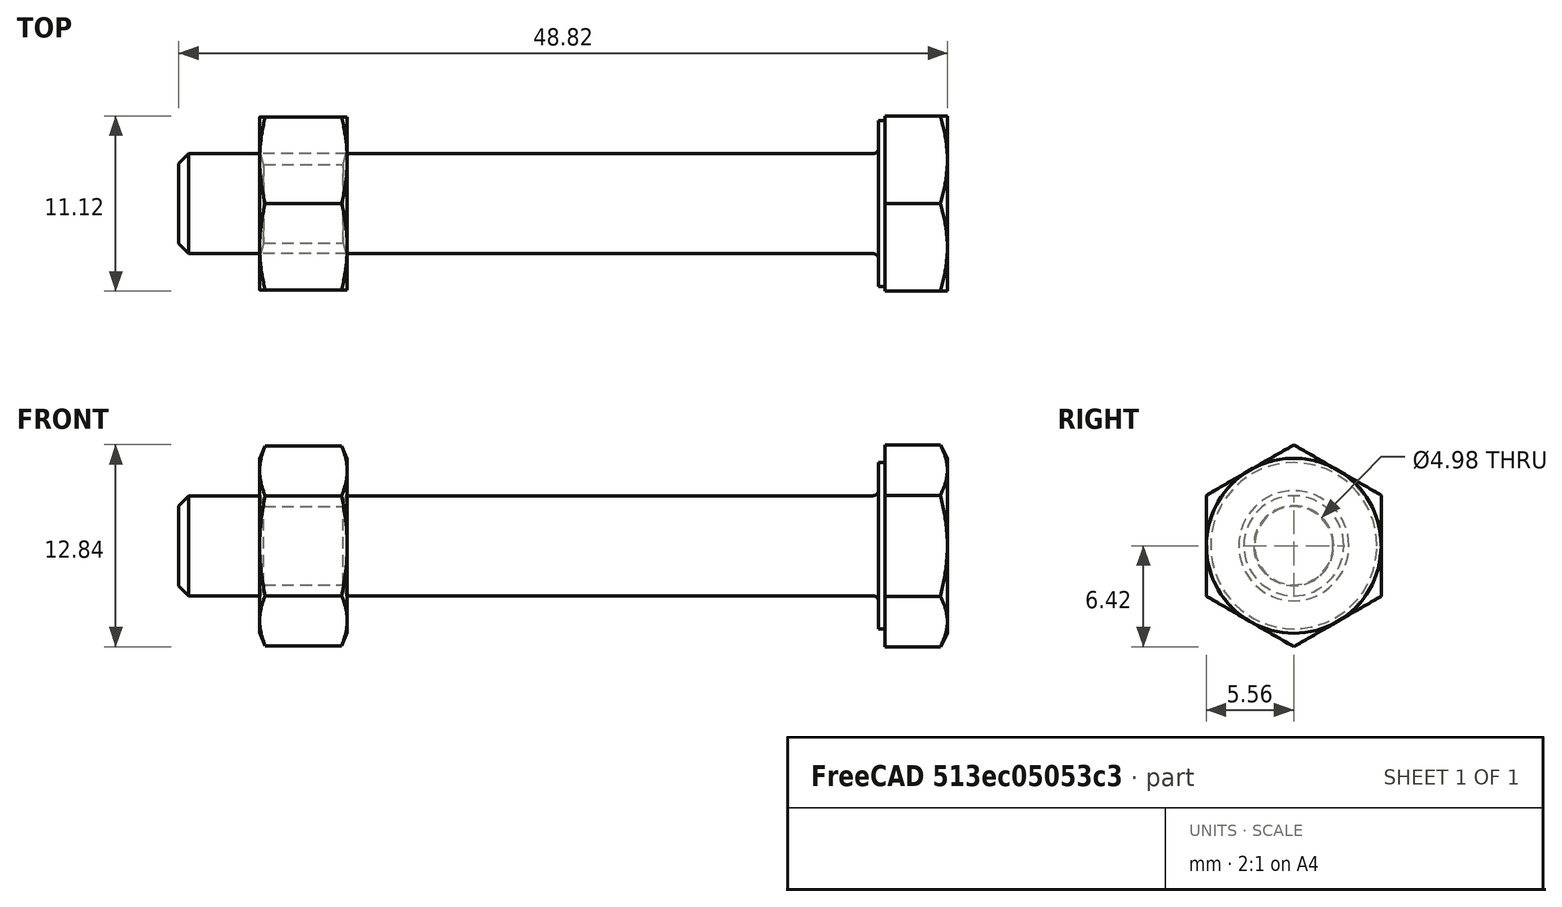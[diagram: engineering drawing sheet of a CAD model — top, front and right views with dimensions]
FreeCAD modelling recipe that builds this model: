
FCSTD DOCUMENT  (FreeCAD 0.20R29177 +426 (Git))
Label: ASM_Base
License: All rights reserved
LicenseURL: http://en.wikipedia.org/wiki/All_rights_reserved
objects: App::Link×10, App::DocumentObjectGroup×3, Part::FeaturePython×2, PartDesign::CoordinateSystem×1, App::FeaturePython×1, App::Part×1
note: 3 computed .brp shape members not serialized (recipe doc carries the construction recipe); baked Part::Feature solids carry a one-line shape summary decoded from their .brp
EXTERNAL_REF file=PillowBlock.FCStd obj=Sketch001
EXTERNAL_REF file=StrutChannelHalf.FCStd obj=LCS_Face
EXTERNAL_REF file=StrutChannelHalf.FCStd obj=Assembly
EXTERNAL_REF file=PillowBlock.FCStd obj=LCS_Origin
EXTERNAL_REF file=PillowBlock.FCStd obj=Assembly
EXTERNAL_REF file=PipeNipple.FCStd obj=LCS_root
EXTERNAL_REF file=PipeNipple.FCStd obj=Body
EXTERNAL_REF file=Arm.FCStd obj=LCS_Center
EXTERNAL_REF file=PipeNipple.FCStd obj=LCS_end
EXTERNAL_REF file=Arm.FCStd obj=Part
EXTERNAL_REF file=SlipRing.FCStd obj=LCS_Origin
EXTERNAL_REF file=SlipRing.FCStd obj=Assembly
EXTERNAL_REF file=Arm.FCStd obj=LCS_End2
EXTERNAL_REF file=Board.FCStd obj=LCS_Center
EXTERNAL_REF file=Board.FCStd obj=Part
EXTERNAL_REF file=ASM_Stepper.FCStd obj=LCS_Origin
EXTERNAL_REF file=ASM_Stepper.FCStd obj=Assembly
EXTERNAL_REF file=Platform.FCStd obj=LCS_Origin
EXTERNAL_REF file=Platform.FCStd obj=Assembly
EXTERNAL_REF file=Platform.FCStd obj=Pad
EXTERNAL_REF file=PlayStation5.FCStd obj=LCS_Origin
EXTERNAL_REF file=PlayStation5.FCStd obj=Assembly

FEATURE [App::DocumentObjectGroup] Parts
FEATURE [PartDesign::CoordinateSystem] LCS_Origin
  AttacherType = Attacher::AttachEngine3D
  MapMode = 2
  Support = -> [X_Axis]
FEATURE [App::DocumentObjectGroup] Constraints
FEATURE [App::FeaturePython] Variables  # WARN: FeaturePython — macro-defined, semantics opaque (R4)
  PillowBlockBoltSpacing = 102.01
  Type = App::PropertyContainer
  expr: PillowBlockBoltSpacing = <<PillowBlock>>#<<PadSketch>>.Constraints.MountHoleSpacing
FEATURE [App::DocumentObjectGroup] Configurations
FEATURE [App::Link] StrutChannelHalf_1
  AttachedBy = #LCS_Face
  AttachedTo = Parent Assembly#LCS_Origin
  AttachmentOffset = pos=(-51.005,0,0) rot=(1,0,0;4.71239rad)
  LinkPlacement = pos=(-51.005,4.6e-15,20.64) rot=(1,0,0;4.71239rad)
  LinkedObject = -> <external StrutChannelHalf.FCStd>#Assembly
  Placement = pos=(-51.005,4.6e-15,20.64) rot=(1,0,0;4.71239rad)
  SolverId = Asm4EE
  expr: .AttachmentOffset.Base.x = <<Variables>>.PillowBlockBoltSpacing / -2
  expr: Placement = LCS_Origin.Placement * AttachmentOffset * StrutChannelHalf#LCS_Face.Placement ^ -1
FEATURE [App::Link] StrutChannelHalf_002
  AttachedBy = #LCS_Face
  AttachedTo = Parent Assembly#LCS_Origin
  AttachmentOffset = pos=(51.005,0,0) rot=(1,0,0;4.71239rad)
  LinkPlacement = pos=(51.005,4.6e-15,20.64) rot=(1,0,0;4.71239rad)
  LinkedObject = -> <external StrutChannelHalf.FCStd>#Assembly
  Placement = pos=(51.005,4.6e-15,20.64) rot=(1,0,0;4.71239rad)
  SolverId = Asm4EE
  expr: .AttachmentOffset.Base.x = <<Variables>>.PillowBlockBoltSpacing / 2
  expr: Placement = LCS_Origin.Placement * AttachmentOffset * StrutChannelHalf#LCS_Face.Placement ^ -1
FEATURE [App::Link] PillowBlock
  AttachedBy = #LCS_Origin
  AttachedTo = Parent Assembly#LCS_Origin
  AttachmentOffset = pos=(0,0,0) rot=(1,0,0;3.14159rad)
  LinkPlacement = pos=(0,0,0) rot=(1,0,0;3.14159rad)
  LinkedObject = -> <external PillowBlock.FCStd>#Assembly
  Placement = pos=(0,0,0) rot=(1,0,0;3.14159rad)
  SolverId = Asm4EE
  expr: Placement = LCS_Origin.Placement * AttachmentOffset * PillowBlock#LCS_Origin.Placement ^ -1
FEATURE [App::Link] Spindle
  AttachedBy = #LCS_root
  AttachedTo = Parent Assembly#LCS_Origin
  AttachmentOffset = pos=(0,0,10) rot=(1,0,0;3.14159rad)
  LinkPlacement = pos=(0,0,10) rot=(1,0,0;3.14159rad)
  LinkedObject = -> <external PipeNipple.FCStd>#Body
  Placement = pos=(0,0,10) rot=(1,0,0;3.14159rad)
  SolverId = Asm4EE
  expr: Placement = LCS_Origin.Placement * AttachmentOffset * PipeNipple#LCS_root.Placement ^ -1
FEATURE [App::Link] Arm
  AttachedBy = #LCS_Center
  AttachedTo = Spindle#LCS_end
  AttachmentOffset = pos=(0,-350,-14) rot=(-0.57735,-0.57735,0.57735;4.18879rad)
  LinkPlacement = pos=(0,350,-116) rot=(-0.57735,-0.57735,-0.57735;2.0944rad)
  LinkedObject = -> <external Arm.FCStd>#Part
  Placement = pos=(0,350,-116) rot=(-0.57735,-0.57735,-0.57735;2.0944rad)
  SolverId = Asm4EE
  expr: Placement = Spindle.Placement * PipeNipple#LCS_end.Placement * AttachmentOffset * Arm#LCS_Center.Placement ^ -1
FEATURE [Part::FeaturePython] Screw  label="1/4inx1 3/4in-Screw"  # Fasteners workbench fastener (typed FeaturePython)
  AttachedBy = Origin
  AttachedTo = Spindle#LCS_end
  AttachmentOffset = pos=(17,0,-16) rot=(0,-1,0;4.71239rad)
  Placement = pos=(17,-1.52e-14,-114) rot=(-0.707107,0,-0.707107;3.14159rad)
  SolverId = Asm4EE
  diameter = 1
  invert = false
  leftHanded = false
  length = 7
  lengthCustom = 44.45
  matchOuter = false
  offset = 0
  thread = false
  type = 1
  expr: Placement = Spindle.Placement * PipeNipple#LCS_end.Placement * AttachmentOffset
FEATURE [Part::FeaturePython] Nut  label="1/4in-Nut"  # Fasteners workbench fastener (typed FeaturePython)
  Placement = pos=(-22.315,-1.52e-14,-114) rot=(0,1,0;1.5708rad)
  baseObject = -> Screw [Edge41]
  diameter = 1
  invert = false
  leftHanded = false
  matchOuter = false
  offset = 4.5
  thread = false
  type = 5
FEATURE [App::Link] SlipRing
  AttachedBy = #LCS_Origin
  AttachedTo = Spindle#LCS_root
  LinkPlacement = pos=(0,0,10) rot=(1,0,0;3.14159rad)
  LinkedObject = -> <external SlipRing.FCStd>#Assembly
  Placement = pos=(0,0,10) rot=(1,0,0;3.14159rad)
  SolverId = Asm4EE
  expr: Placement = Spindle.Placement * PipeNipple#LCS_root.Placement * AttachmentOffset * SlipRing#LCS_Origin.Placement ^ -1
FEATURE [App::Link] MotorBoard
  AttachedBy = #LCS_Center
  AttachedTo = Arm#LCS_End2
  AttachmentOffset = pos=(11,0,-9.5) rot=(0.57735,0.57735,0.57735;2.0944rad)
  LinkPlacement = pos=(1.662e-13,-409.5,-105) rot=(0,0,1;0rad)
  LinkedObject = -> <external Board.FCStd>#Part
  Placement = pos=(1.662e-13,-409.5,-105) rot=(0,0,1;0rad)
  SolverId = Asm4EE
  expr: Placement = Arm.Placement * Arm#LCS_End2.Placement * AttachmentOffset * Board#LCS_Center.Placement ^ -1
FEATURE [App::Link] ASM_Stepper
  AttachedBy = #LCS_Origin
  AttachedTo = MotorBoard#LCS_Center
  AttachmentOffset = pos=(0,-9.5,13) rot=(1,0,0;1.5708rad)
  LinkPlacement = pos=(1.611e-13,-419,-92) rot=(1,0,0;1.5708rad)
  LinkedObject = -> <external ASM_Stepper.FCStd>#Assembly
  Placement = pos=(1.611e-13,-419,-92) rot=(1,0,0;1.5708rad)
  SolverId = Asm4EE
  expr: Placement = MotorBoard.Placement * Board#LCS_Center.Placement * AttachmentOffset * ASM_Stepper#LCS_Origin.Placement ^ -1
FEATURE [App::Link] Platform
  AttachedBy = #LCS_Origin
  AttachedTo = Arm#LCS_End2
  AttachmentOffset = pos=(19.05,0,170) rot=(0.57735,0.57735,0.57735;2.0944rad)
  LinkPlacement = pos=(1.246e-13,-230,-96.95) rot=(0,0,1;0rad)
  LinkedObject = -> <external Platform.FCStd>#Assembly
  Placement = pos=(1.246e-13,-230,-96.95) rot=(0,0,1;0rad)
  SolverId = Asm4EE
  expr: Placement = Arm.Placement * Arm#LCS_End2.Placement * AttachmentOffset * Platform#LCS_Origin.Placement ^ -1
FEATURE [App::Link] PlayStation5
  AttachedBy = #LCS_Origin
  AttachedTo = Platform#LCS_Origin
  AttachmentOffset = pos=(0,0,6.35) rot=(0,0,1;1.5708rad)
  LinkPlacement = pos=(1.221e-13,-230,-90.6) rot=(0,0,1;1.5708rad)
  LinkedObject = -> <external PlayStation5.FCStd>#Assembly
  Placement = pos=(1.221e-13,-230,-90.6) rot=(0,0,1;1.5708rad)
  SolverId = Asm4EE
  expr: .AttachmentOffset.Base.z = <<Platform>>#<<Pad>>.Length
  expr: Placement = Platform.Placement * Platform#LCS_Origin.Placement * AttachmentOffset * PlayStation5#LCS_Origin.Placement ^ -1
FEATURE [App::Part] Assembly
  AssemblyType = Part::Link
  Group = -> [LCS_Origin,Constraints,Variables,Configurations,StrutChannelHalf_1,StrutChannelHalf_002,PillowBlock,Spindle,Arm,Screw,Nut,SlipRing,MotorBoard,ASM_Stepper,Platform,PlayStation5]
  Origin = -> Origin
  Type = Assembly

RESOLVED EXTERNAL PARTS (link-assembly join: the EXTERNAL_REF files above that resolve inside this repo's crawl, each included once):
---- part ASM_Stepper.FCStd = doc fcstd_8e194f77de06 ----
FCSTD DOCUMENT  (FreeCAD 0.20R29177 +426 (Git))
Label: ASM_Stepper
License: All rights reserved
LicenseURL: http://en.wikipedia.org/wiki/All_rights_reserved
objects: App::Link×4, App::DocumentObjectGroup×3, PartDesign::CoordinateSystem×1, App::FeaturePython×1, App::Part×1
note: 1 computed .brp shape members not serialized (recipe doc carries the construction recipe); baked Part::Feature solids carry a one-line shape summary decoded from their .brp
EXTERNAL_REF file=Stepper17BracketFlat.FCStd obj=LCS_Mount
EXTERNAL_REF file=Stepper17BracketFlat.FCStd obj=Assembly
EXTERNAL_REF file=Stepper17.FCStd obj=LCS_mount
EXTERNAL_REF file=Stepper17BracketFlat.FCStd obj=LCS_Origin
EXTERNAL_REF file=Stepper17.FCStd obj=Body
EXTERNAL_REF file=FlangeHub5mm.FCStd obj=LCS_Origin
EXTERNAL_REF file=FlangeHub5mm.FCStd obj=Assembly
EXTERNAL_REF file=Wheel.FCStd obj=LCS_Origin
EXTERNAL_REF file=Wheel.FCStd obj=Assembly

FEATURE [App::DocumentObjectGroup] Parts
FEATURE [PartDesign::CoordinateSystem] LCS_Origin
  AttacherType = Attacher::AttachEngine3D
  MapMode = 2
  Support = -> [X_Axis]
FEATURE [App::DocumentObjectGroup] Constraints
FEATURE [App::FeaturePython] Variables  # WARN: FeaturePython — macro-defined, semantics opaque (R4)
  Type = App::PropertyContainer
FEATURE [App::DocumentObjectGroup] Configurations
FEATURE [App::Link] Stepper17BracketFlat
  AttachedBy = #LCS_Mount
  AttachedTo = Parent Assembly#LCS_Origin
  LinkPlacement = pos=(0,53.75,0) rot=(0,0,1;0rad)
  LinkedObject = -> <external Stepper17BracketFlat.FCStd>#Assembly
  Placement = pos=(0,53.75,0) rot=(0,0,1;0rad)
  SolverId = Asm4EE
  expr: Placement = LCS_Origin.Placement * AttachmentOffset * Stepper17BracketFlat#LCS_Mount.Placement ^ -1
FEATURE [App::Link] Stepper
  AttachedBy = #LCS_mount
  AttachedTo = Stepper17BracketFlat#LCS_Origin
  AttachmentOffset = pos=(0,0,0) rot=(0,1,0;3.14159rad)
  LinkPlacement = pos=(0,53.75,0) rot=(0,1,0;3.14159rad)
  LinkedObject = -> <external Stepper17.FCStd>#Body
  Placement = pos=(0,53.75,0) rot=(0,1,0;3.14159rad)
  SolverId = Asm4EE
  expr: Placement = Stepper17BracketFlat.Placement * Stepper17BracketFlat#LCS_Origin.Placement * AttachmentOffset * Stepper17#LCS_mount.Placement ^ -1
FEATURE [App::Link] FlangeHub5mm
  AttachedBy = #LCS_Origin
  AttachedTo = Stepper#LCS_mount
  AttachmentOffset = pos=(0,0,-14) rot=(1,0,0;3.14159rad)
  LinkPlacement = pos=(-1.7e-15,53.75,14) rot=(0,0,-1;3.14159rad)
  LinkedObject = -> <external FlangeHub5mm.FCStd>#Assembly
  Placement = pos=(-1.7e-15,53.75,14) rot=(0,0,-1;3.14159rad)
  SolverId = Asm4EE
  expr: Placement = Stepper.Placement * Stepper17#LCS_mount.Placement * AttachmentOffset * FlangeHub5mm#LCS_Origin.Placement ^ -1
FEATURE [App::Link] Wheel
  AttachedBy = #LCS_Origin
  AttachedTo = FlangeHub5mm#LCS_Origin
  AttachmentOffset = pos=(0,0,0) rot=(0,1,0;3.14159rad)
  LinkPlacement = pos=(-1.7e-15,53.75,14) rot=(1,0,0;3.14159rad)
  LinkedObject = -> <external Wheel.FCStd>#Assembly
  Placement = pos=(-1.7e-15,53.75,14) rot=(1,0,0;3.14159rad)
  SolverId = Asm4EE
  expr: Placement = FlangeHub5mm.Placement * FlangeHub5mm#LCS_Origin.Placement * AttachmentOffset * Wheel#LCS_Origin.Placement ^ -1
FEATURE [App::Part] Assembly
  AssemblyType = Part::Link
  Group = -> [LCS_Origin,Constraints,Variables,Configurations,Stepper17BracketFlat,Stepper,FlangeHub5mm,Wheel]
  Origin = -> Origin
  Type = Assembly
---- part Arm.FCStd = doc fcstd_95bc69fd2989 ----
FCSTD DOCUMENT  (FreeCAD 0.20R29177 +426 (Git))
Label: Arm
License: All rights reserved
LicenseURL: http://en.wikipedia.org/wiki/All_rights_reserved
objects: PartDesign::CoordinateSystem×3, Sketcher::SketchObject×1, App::FeaturePython×1, PartDesign::Pad×1, PartDesign::Body×1, App::Part×1
note: 7 computed .brp shape members not serialized (recipe doc carries the construction recipe); baked Part::Feature solids carry a one-line shape summary decoded from their .brp

FEATURE [Sketcher::SketchObject] Sketch
  FullyConstrained = true
  MapMode = 5
  Support = -> [XY_Plane001]
  expr: Constraints[16] = <<Variables>>.FilletRadius
  expr: Constraints[18] = <<Variables>>.Dim1
  expr: Constraints[19] = <<Variables>>.Dim2
  sketch-geometry (9):
    g0: LineSegment StartX=-19.05 StartY=9.025 StartZ=0 EndX=-19.05 EndY=-9.025 EndZ=0
    g1: LineSegment StartX=-18.55 StartY=-9.525 StartZ=0 EndX=18.55 EndY=-9.525 EndZ=0
    g2: LineSegment StartX=19.05 StartY=-9.025 StartZ=0 EndX=19.05 EndY=9.025 EndZ=0
    g3: LineSegment StartX=18.55 StartY=9.525 StartZ=0 EndX=-18.55 EndY=9.525 EndZ=0
    g4: GeomPoint X=0 Y=0 Z=0
    g5: ArcOfCircle CenterX=-18.55 CenterY=9.025 CenterZ=0 NormalX=0 NormalY=0 NormalZ=1 AngleXU=0 Radius=0.5 StartAngle=1.5708 EndAngle=3.14159
    g6: ArcOfCircle CenterX=-18.55 CenterY=-9.025 CenterZ=0 NormalX=0 NormalY=0 NormalZ=1 AngleXU=0 Radius=0.5 StartAngle=3.14159 EndAngle=4.71239
    g7: ArcOfCircle CenterX=18.55 CenterY=9.025 CenterZ=0 NormalX=0 NormalY=0 NormalZ=1 AngleXU=0 Radius=0.5 StartAngle=1.95e-14 EndAngle=1.5708
    g8: ArcOfCircle CenterX=18.55 CenterY=-9.025 CenterZ=0 NormalX=0 NormalY=0 NormalZ=1 AngleXU=0 Radius=0.5 StartAngle=4.71239 EndAngle=6.28319
  constraints (20):
    c: Horizontal(g1)
    c: Horizontal(g3)
    c: Vertical(g0)
    c: Vertical(g2)
    c: Coincident(g4,g-1)
    c: Tangent(g3,g5) = -1.5708
    c: Tangent(g0,g5) = -1.5708
    c: Tangent(g0,g6) = -1.5708
    c: Tangent(g1,g6) = -1.5708
    c: Tangent(g3,g7) = -1.5708
    c: Tangent(g2,g7) = -1.5708
    c: Tangent(g2,g8) = -1.5708
    c: Tangent(g1,g8) = -1.5708
    c: Equal(g8,g7)
    c: Equal(g7,g5)
    c: Equal(g5,g6)
    c: Radius(g7) = 0.5
    c: Symmetric(g7,g6,g4)
    c: DistanceY(g1,g3) = 19.05
    c: DistanceX(g0,g2) = 38.1
FEATURE [App::FeaturePython] Variables  # WARN: FeaturePython — macro-defined, semantics opaque (R4)
  Dim1 = 19.05
  Dim2 = 38.1
  FilletRadius = 0.5
  Length = 1500
  Type = App::PropertyContainer
FEATURE [PartDesign::Pad] Pad
  Direction = (0,0,1)
  Length = 1500
  Length2 = 10
  Midplane = true
  Profile = -> Sketch
  ReferenceAxis = -> Sketch [N_Axis]
  Type = 0
  expr: Length = <<Variables>>.Length
FEATURE [PartDesign::Body] Body
  Group = -> [Sketch,Pad]
  Origin = -> Origin001
  Tip = -> Pad
FEATURE [PartDesign::CoordinateSystem] LCS_Center
  AttacherType = Attacher::AttachEngine3D
  MapMode = 2
  Support = -> [XY_Plane]
FEATURE [PartDesign::CoordinateSystem] LCS_End1
  AttacherType = Attacher::AttachEngine3D
  AttachmentOffset = pos=(0,0,750) rot=(0,0,1;0rad)
  MapMode = 2
  Placement = pos=(0,0,750) rot=(0,0,1;0rad)
  Support = -> [XY_Plane]
  expr: .AttachmentOffset.Base.z = <<Variables>>.Length / 2
FEATURE [PartDesign::CoordinateSystem] LCS_End2
  AttacherType = Attacher::AttachEngine3D
  AttachmentOffset = pos=(0,0,-750) rot=(0,0,1;0rad)
  MapMode = 2
  Placement = pos=(0,0,-750) rot=(0,0,1;0rad)
  Support = -> [XY_Plane]
  expr: .AttachmentOffset.Base.z = <<Variables>>.Length / -2
FEATURE [App::Part] Part
  Group = -> [Body,Variables,LCS_Center,LCS_End1,LCS_End2]
  Origin = -> Origin
  Type = Asm4::VariantLink
---- part Board.FCStd = doc fcstd_57f5a6b6b108 ----
FCSTD DOCUMENT  (FreeCAD 0.20R29177 +426 (Git))
Label: Board
License: All rights reserved
LicenseURL: http://en.wikipedia.org/wiki/All_rights_reserved
objects: PartDesign::CoordinateSystem×3, Sketcher::SketchObject×1, App::FeaturePython×1, PartDesign::Pad×1, PartDesign::Body×1, App::Part×1
note: 7 computed .brp shape members not serialized (recipe doc carries the construction recipe); baked Part::Feature solids carry a one-line shape summary decoded from their .brp

FEATURE [Sketcher::SketchObject] Sketch
  FullyConstrained = true
  MapMode = 5
  Support = -> [XY_Plane001]
  expr: Constraints[16] = <<Variables>>.FilletRadius
  expr: Constraints[18] = <<Variables>>.Dim1
  expr: Constraints[19] = <<Variables>>.Dim2
  sketch-geometry (9):
    g0: LineSegment StartX=-19.05 StartY=9.025 StartZ=0 EndX=-19.05 EndY=-9.025 EndZ=0
    g1: LineSegment StartX=-18.55 StartY=-9.525 StartZ=0 EndX=18.55 EndY=-9.525 EndZ=0
    g2: LineSegment StartX=19.05 StartY=-9.025 StartZ=0 EndX=19.05 EndY=9.025 EndZ=0
    g3: LineSegment StartX=18.55 StartY=9.525 StartZ=0 EndX=-18.55 EndY=9.525 EndZ=0
    g4: GeomPoint X=0 Y=0 Z=0
    g5: ArcOfCircle CenterX=-18.55 CenterY=9.025 CenterZ=0 NormalX=0 NormalY=0 NormalZ=1 AngleXU=0 Radius=0.5 StartAngle=1.5708 EndAngle=3.14159
    g6: ArcOfCircle CenterX=-18.55 CenterY=-9.025 CenterZ=0 NormalX=0 NormalY=0 NormalZ=1 AngleXU=0 Radius=0.5 StartAngle=3.14159 EndAngle=4.71239
    g7: ArcOfCircle CenterX=18.55 CenterY=9.025 CenterZ=0 NormalX=0 NormalY=0 NormalZ=1 AngleXU=0 Radius=0.5 StartAngle=-8.4555e-12 EndAngle=1.5708
    g8: ArcOfCircle CenterX=18.55 CenterY=-9.025 CenterZ=0 NormalX=0 NormalY=0 NormalZ=1 AngleXU=0 Radius=0.5 StartAngle=4.71239 EndAngle=6.28319
  constraints (20):
    c: Horizontal(g1)
    c: Horizontal(g3)
    c: Vertical(g0)
    c: Vertical(g2)
    c: Coincident(g4,g-1)
    c: Tangent(g3,g5) = -1.5708
    c: Tangent(g0,g5) = -1.5708
    c: Tangent(g0,g6) = -1.5708
    c: Tangent(g1,g6) = -1.5708
    c: Tangent(g3,g7) = -1.5708
    c: Tangent(g2,g7) = -1.5708
    c: Tangent(g2,g8) = -1.5708
    c: Tangent(g1,g8) = -1.5708
    c: Equal(g8,g7)
    c: Equal(g7,g5)
    c: Equal(g5,g6)
    c: Radius(g7) = 0.5
    c: Symmetric(g7,g6,g4)
    c: DistanceY(g1,g3) = 19.05
    c: DistanceX(g0,g2) = 38.1
FEATURE [App::FeaturePython] Variables  # WARN: FeaturePython — macro-defined, semantics opaque (R4)
  Dim1 = 19.05
  Dim2 = 38.1
  FilletRadius = 0.5
  Length = 60
  Type = App::PropertyContainer
FEATURE [PartDesign::Pad] Pad
  Direction = (0,0,1)
  Length = 60
  Length2 = 10
  Midplane = true
  Profile = -> Sketch
  ReferenceAxis = -> Sketch [N_Axis]
  Type = 0
  expr: Length = <<Variables>>.Length
FEATURE [PartDesign::Body] Body
  Group = -> [Sketch,Pad]
  Origin = -> Origin001
  Tip = -> Pad
FEATURE [PartDesign::CoordinateSystem] LCS_Center
  AttacherType = Attacher::AttachEngine3D
  MapMode = 2
  Support = -> [XY_Plane]
FEATURE [PartDesign::CoordinateSystem] LCS_End1
  AttacherType = Attacher::AttachEngine3D
  AttachmentOffset = pos=(0,0,30) rot=(0,0,1;0rad)
  MapMode = 2
  Placement = pos=(0,0,30) rot=(0,0,1;0rad)
  Support = -> [XY_Plane]
  expr: .AttachmentOffset.Base.z = <<Variables>>.Length / 2
FEATURE [PartDesign::CoordinateSystem] LCS_End2
  AttacherType = Attacher::AttachEngine3D
  AttachmentOffset = pos=(0,0,-30) rot=(0,0,1;0rad)
  MapMode = 2
  Placement = pos=(0,0,-30) rot=(0,0,1;0rad)
  Support = -> [XY_Plane]
  expr: .AttachmentOffset.Base.z = <<Variables>>.Length / -2
FEATURE [App::Part] Part
  Group = -> [Body,Variables,LCS_Center,LCS_End1,LCS_End2]
  Origin = -> Origin
  Type = Asm4::VariantLink
---- part PillowBlock.FCStd = doc fcstd_4e686e80bc07 ----
FCSTD DOCUMENT  (FreeCAD 0.20R29177 +426 (Git))
Label: PillowBlock
License: All rights reserved
LicenseURL: http://en.wikipedia.org/wiki/All_rights_reserved
objects: App::DocumentObjectGroup×4, Part::FeaturePython×4, Sketcher::SketchObject×2, PartDesign::Revolution×1, PartDesign::Pad×1, PartDesign::Body×1, PartDesign::CoordinateSystem×1, App::FeaturePython×1, App::Part×1
note: 12 computed .brp shape members not serialized (recipe doc carries the construction recipe); baked Part::Feature solids carry a one-line shape summary decoded from their .brp

FEATURE [Sketcher::SketchObject] Sketch
  FullyConstrained = true
  MapMode = 5
  Placement = pos=(0,0,0) rot=(1,0,0;1.5708rad)
  Support = -> [XZ_Plane]
  sketch-geometry (6):
    g0: LineSegment StartX=19.05 StartY=0 StartZ=0 EndX=19.05 EndY=51.2064 EndZ=0
    g1: LineSegment StartX=43.4 StartY=36.068 StartZ=0 EndX=51.05 EndY=0 EndZ=0
    g2: LineSegment StartX=51.05 StartY=0 StartZ=0 EndX=19.05 EndY=0 EndZ=0
    g3: LineSegment StartX=43.4 StartY=36.068 StartZ=0 EndX=25.4 EndY=36.068 EndZ=0
    g4: LineSegment StartX=25.4 StartY=36.068 StartZ=0 EndX=25.4 EndY=51.2064 EndZ=0
    g5: LineSegment StartX=25.4 StartY=51.2064 StartZ=0 EndX=19.05 EndY=51.2064 EndZ=0
  constraints (18):
    c: PointOnObject(g0,g-1)
    c: Vertical(g0)
    c: PointOnObject(g2,g-1)
    c: Coincident(g2,g0)
    c: Coincident(g1,g2)
    c: DistanceX(g-1,g0) = 19.05  'ShaftRadius'
    c: Coincident(g1,g3)
    c: Horizontal(g3)
    c: Coincident(g3,g4)
    c: Vertical(g4)
    c: Coincident(g4,g5)
    c: Horizontal(g5)
    c: Coincident(g5,g0)
    c: DistanceY(g1,g1) = 36.068
    c: DistanceY(g1,g4) = 51.2064
    c: DistanceX(g5,g5) = 6.35
    c: DistanceX(g3,g3) = 18
    c: DistanceX(g2,g2) = 32
FEATURE [PartDesign::Revolution] Revolution
  Angle = 360
  Axis = (0,-2e-16,1)
  Base = (0,0,0)
  Placement = pos=(0,0,0) rot=(1,0,0;1.5708rad)
  Profile = -> Sketch
  ReferenceAxis = -> Sketch [V_Axis]
  Reversed = true
FEATURE [Sketcher::SketchObject] Sketch001  label="PadSketch"
  FullyConstrained = true
  MapMode = 5
  Support = -> [XY_Plane]
  expr: Constraints[32] = <<Sketch>>.Constraints.ShaftRadius
  sketch-geometry (15):
    g0: ArcOfCircle CenterX=-51.005 CenterY=51.005 CenterZ=0 NormalX=0 NormalY=0 NormalZ=1 AngleXU=0 Radius=14.0825 StartAngle=1.5708 EndAngle=3.14159
    g1: LineSegment StartX=-51.005 StartY=65.0875 StartZ=0 EndX=51.005 EndY=65.0875 EndZ=0
    g2: ArcOfCircle CenterX=51.005 CenterY=51.005 CenterZ=0 NormalX=0 NormalY=0 NormalZ=1 AngleXU=0 Radius=14.0825 StartAngle=0 EndAngle=1.5708
    g3: LineSegment StartX=65.0875 StartY=51.005 StartZ=0 EndX=65.0875 EndY=-51.005 EndZ=0
    g4: ArcOfCircle CenterX=51.005 CenterY=-51.005 CenterZ=0 NormalX=0 NormalY=0 NormalZ=1 AngleXU=0 Radius=14.0825 StartAngle=4.71239 EndAngle=6.28319
    g5: LineSegment StartX=51.005 StartY=-65.0875 StartZ=0 EndX=-51.005 EndY=-65.0875 EndZ=0
    g6: ArcOfCircle CenterX=-51.005 CenterY=-51.005 CenterZ=0 NormalX=0 NormalY=0 NormalZ=1 AngleXU=0 Radius=14.0825 StartAngle=3.14159 EndAngle=4.71239
    g7: LineSegment StartX=-65.0875 StartY=-51.005 StartZ=0 EndX=-65.0875 EndY=51.005 EndZ=0
    g8: GeomPoint X=-65.0875 Y=65.0875 Z=0
    g9: GeomPoint X=65.0875 Y=-65.0875 Z=0
    g10: Circle CenterX=51.005 CenterY=51.005 CenterZ=0 NormalX=0 NormalY=0 NormalZ=1 AngleXU=0 Radius=7
    g11: Circle CenterX=-51.005 CenterY=51.005 CenterZ=0 NormalX=0 NormalY=0 NormalZ=1 AngleXU=0 Radius=7
    g12: Circle CenterX=-51.005 CenterY=-51.005 CenterZ=0 NormalX=0 NormalY=0 NormalZ=1 AngleXU=0 Radius=7
    g13: Circle CenterX=51.005 CenterY=-51.005 CenterZ=0 NormalX=0 NormalY=0 NormalZ=1 AngleXU=0 Radius=7
    g14: Circle CenterX=0 CenterY=0 CenterZ=0 NormalX=0 NormalY=0 NormalZ=1 AngleXU=0 Radius=19.05
  constraints (33):
    c: Tangent(g0,g1) = 1.5708
    c: Tangent(g1,g2) = 1.5708
    c: Tangent(g2,g3) = 1.5708
    c: Tangent(g3,g4) = 1.5708
    c: Tangent(g4,g5) = 1.5708
    c: Tangent(g5,g6) = 1.5708
    c: Tangent(g6,g7) = 1.5708
    c: Tangent(g7,g0) = 1.5708
    c: Horizontal(g1)
    c: Horizontal(g5)
    c: Vertical(g3)
    c: Vertical(g7)
    c: Equal(g0,g2)
    c: Equal(g2,g4)
    c: Equal(g4,g6)
    c: PointOnObject(g8,g1)
    c: PointOnObject(g8,g7)
    c: PointOnObject(g9,g3)
    c: PointOnObject(g9,g5)
    c: Equal(g1,g3)
    c: Symmetric(g2,g6,g-1)
    c: DistanceY(g4,g2) = 102.01  'MountHoleSpacing'
    c: Coincident(g10,g2)
    c: Coincident(g11,g0)
    c: Coincident(g12,g6)
    c: Coincident(g13,g4)
    c: Equal(g13,g12)
    c: Equal(g12,g11)
    c: Equal(g11,g10)
    c: Diameter(g10) = 14
    c: DistanceY(g4,g1) = 130.175
    c: Coincident(g14,g-1)
    c: Radius(g14) = 19.05
FEATURE [PartDesign::Pad] Pad
  BaseFeature = -> Revolution
  Direction = (0,0,1)
  Length = 15.875
  Length2 = 10
  Placement = pos=(0,0,0) rot=(1,0,0;1.5708rad)
  Profile = -> Sketch001
  ReferenceAxis = -> Sketch001 [N_Axis]
  Type = 0
FEATURE [PartDesign::Body] Body
  Group = -> [Sketch,Revolution,Sketch001,Pad]
  Origin = -> Origin
  Tip = -> Pad
FEATURE [App::DocumentObjectGroup] Parts
FEATURE [PartDesign::CoordinateSystem] LCS_Origin
  AttacherType = Attacher::AttachEngine3D
  MapMode = 2
  Support = -> [X_Axis001]
FEATURE [App::FeaturePython] Variables  # WARN: FeaturePython — macro-defined, semantics opaque (R4)
  Type = App::PropertyContainer
FEATURE [App::DocumentObjectGroup] Constraints
FEATURE [App::DocumentObjectGroup] Configurations
FEATURE [Part::FeaturePython] Screw  label="1/2inx1 1/4in-Screw"  # Fasteners workbench fastener (typed FeaturePython)
  Placement = pos=(51.005,-51.005,15.875) rot=(0,0,1;0rad)
  baseObject = -> Body [Edge13]
  diameter = 5
  invert = false
  leftHanded = false
  length = 1
  lengthCustom = 31.75
  matchOuter = false
  offset = 0
  thread = false
  type = 1
FEATURE [Part::FeaturePython] Screw001  label="1/2inx1 1/4in-Screw004"  # Fasteners workbench fastener (typed FeaturePython)
  Placement = pos=(-51.005,-51.005,15.875) rot=(0,0,1;0rad)
  baseObject = -> Body [Edge12]
  diameter = 5
  invert = false
  leftHanded = false
  length = 1
  lengthCustom = 31.75
  matchOuter = false
  offset = 0
  thread = false
  type = 1
FEATURE [Part::FeaturePython] Screw002  label="1/2inx1 1/4in-Screw005"  # Fasteners workbench fastener (typed FeaturePython)
  Placement = pos=(51.005,51.005,15.875) rot=(0,0,1;0rad)
  baseObject = -> Body [Edge15]
  diameter = 5
  invert = false
  leftHanded = false
  length = 1
  lengthCustom = 31.75
  matchOuter = false
  offset = 0
  thread = false
  type = 1
FEATURE [Part::FeaturePython] Screw003  label="1/2inx1 1/4in-Screw006"  # Fasteners workbench fastener (typed FeaturePython)
  Placement = pos=(-51.005,51.005,15.875) rot=(0,0,1;0rad)
  baseObject = -> Body [Edge14]
  diameter = 5
  invert = false
  leftHanded = false
  length = 1
  lengthCustom = 31.75
  matchOuter = false
  offset = 0
  thread = false
  type = 1
FEATURE [App::DocumentObjectGroup] Fasteners
  Group = -> [Screw,Screw001,Screw002,Screw003]
FEATURE [App::Part] Assembly
  AssemblyType = Part::Link
  Group = -> [LCS_Origin,Variables,Constraints,Configurations,Body,Fasteners,Screw,Screw001,Screw002,Screw003]
  Origin = -> Origin001
  Type = Assembly
---- part PipeNipple.FCStd = doc fcstd_835e7702a200 ----
FCSTD DOCUMENT  (FreeCAD 0.20R29177 +426 (Git))
Label: PipeNipple
License: All rights reserved
LicenseURL: http://en.wikipedia.org/wiki/All_rights_reserved
objects: Sketcher::SketchObject×2, PartDesign::CoordinateSystem×2, PartDesign::Pad×1, PartDesign::Pocket×1, PartDesign::Body×1
note: 9 computed .brp shape members not serialized (recipe doc carries the construction recipe); baked Part::Feature solids carry a one-line shape summary decoded from their .brp

FEATURE [Sketcher::SketchObject] Sketch
  FullyConstrained = true
  MapMode = 5
  Support = -> [XY_Plane]
  sketch-geometry (2):
    g0: Circle CenterX=0 CenterY=0 CenterZ=0 NormalX=0 NormalY=0 NormalZ=1 AngleXU=0 Radius=13.3223
    g1: Circle CenterX=0 CenterY=0 CenterZ=0 NormalX=0 NormalY=0 NormalZ=1 AngleXU=0 Radius=16.7005
  constraints (4):
    c: Coincident(g0,g-1)
    c: Coincident(g1,g0)
    c: Diameter(g1) = 33.401
    c: Diameter(g0) = 26.6446
FEATURE [PartDesign::Pad] Pad
  Direction = (0,0,1)
  Length = 140
  Length2 = 10
  Profile = -> Sketch
  ReferenceAxis = -> Sketch [N_Axis]
  Type = 0
FEATURE [PartDesign::CoordinateSystem] LCS_root
  AttacherType = Attacher::AttachEngine3D
  MapMode = 2
  Support = -> [XY_Plane]
FEATURE [PartDesign::CoordinateSystem] LCS_end
  AttacherType = Attacher::AttachEngine3D
  AttachmentOffset = pos=(0,0,140) rot=(0,0,1;0rad)
  MapMode = 2
  Placement = pos=(0,0,140) rot=(0,0,1;0rad)
  Support = -> [LCS_root]
  expr: .AttachmentOffset.Base.z = <<Pad>>.Length
FEATURE [Sketcher::SketchObject] Sketch001  label="ArmPocket"
  AttachmentOffset = pos=(0,140,0) rot=(0,0,1;0rad)
  FullyConstrained = true
  MapMode = 5
  Placement = pos=(0,-3.11e-14,140) rot=(1,0,0;1.5708rad)
  Support = -> [XZ_Plane]
  expr: .AttachmentOffset.Base.y = <<Pad>>.Length
  sketch-geometry (5):
    g0: LineSegment StartX=-10 StartY=-40 StartZ=0 EndX=-10 EndY=0 EndZ=0
    g1: LineSegment StartX=-10 StartY=0 StartZ=0 EndX=10 EndY=0 EndZ=0
    g2: LineSegment StartX=10 StartY=0 StartZ=0 EndX=10 EndY=-40 EndZ=0
    g3: LineSegment StartX=10 StartY=-40 StartZ=0 EndX=-10 EndY=-40 EndZ=0
    g4: GeomPoint X=0 Y=-20 Z=0
  constraints (13):
    c: Coincident(g0,g1)
    c: Coincident(g1,g2)
    c: Coincident(g2,g3)
    c: Coincident(g3,g0)
    c: Horizontal(g1)
    c: Horizontal(g3)
    c: Vertical(g0)
    c: Vertical(g2)
    c: Symmetric(g1,g0,g4)
    c: PointOnObject(g4,g-2)
    c: PointOnObject(g1,g-1)
    c: DistanceX(g3,g3) = 20
    c: DistanceY(g2,g2) = 40
FEATURE [PartDesign::Pocket] Pocket
  BaseFeature = -> Pad
  Direction = (0,1,2e-16)
  Length = 5
  Length2 = 5
  Midplane = true
  Profile = -> Sketch001
  ReferenceAxis = -> Sketch001 [N_Axis]
  Type = 1
FEATURE [PartDesign::Body] Body
  Group = -> [Sketch,Pad,LCS_root,LCS_end,Sketch001,Pocket]
  Origin = -> Origin
  Tip = -> Pocket
---- part Platform.FCStd = doc fcstd_cf6c4a2f501b ----
FCSTD DOCUMENT  (FreeCAD 0.20R29177 +426 (Git))
Label: Platform
License: All rights reserved
LicenseURL: http://en.wikipedia.org/wiki/All_rights_reserved
objects: App::DocumentObjectGroup×3, PartDesign::CoordinateSystem×1, App::FeaturePython×1, Sketcher::SketchObject×1, PartDesign::Pad×1, PartDesign::Body×1, App::Part×1
note: 5 computed .brp shape members not serialized (recipe doc carries the construction recipe); baked Part::Feature solids carry a one-line shape summary decoded from their .brp

FEATURE [App::DocumentObjectGroup] Parts
FEATURE [PartDesign::CoordinateSystem] LCS_Origin
  AttacherType = Attacher::AttachEngine3D
  MapMode = 2
  Support = -> [X_Axis]
FEATURE [App::DocumentObjectGroup] Constraints
FEATURE [App::FeaturePython] Variables  # WARN: FeaturePython — macro-defined, semantics opaque (R4)
  Type = App::PropertyContainer
FEATURE [App::DocumentObjectGroup] Configurations
FEATURE [Sketcher::SketchObject] Sketch
  FullyConstrained = true
  MapMode = 5
  Support = -> [XY_Plane001]
  sketch-geometry (5):
    g0: LineSegment StartX=-197 StartY=135 StartZ=0 EndX=-197 EndY=-135 EndZ=0
    g1: LineSegment StartX=-197 StartY=-135 StartZ=0 EndX=197 EndY=-135 EndZ=0
    g2: LineSegment StartX=197 StartY=-135 StartZ=0 EndX=197 EndY=135 EndZ=0
    g3: LineSegment StartX=197 StartY=135 StartZ=0 EndX=-197 EndY=135 EndZ=0
    g4: GeomPoint X=0 Y=0 Z=0
  constraints (12):
    c: Coincident(g0,g1)
    c: Coincident(g1,g2)
    c: Coincident(g2,g3)
    c: Coincident(g3,g0)
    c: Horizontal(g1)
    c: Horizontal(g3)
    c: Vertical(g0)
    c: Vertical(g2)
    c: Symmetric(g1,g0,g4)
    c: Coincident(g4,g-1)
    c: DistanceX(g3,g3) = 394
    c: DistanceY(g2,g2) = 270
FEATURE [PartDesign::Pad] Pad
  Direction = (0,0,1)
  Length = 6.35
  Length2 = 10
  Profile = -> Sketch
  ReferenceAxis = -> Sketch [N_Axis]
  Type = 0
FEATURE [PartDesign::Body] Body
  Group = -> [Sketch,Pad]
  Origin = -> Origin001
  Tip = -> Pad
FEATURE [App::Part] Assembly
  AssemblyType = Part::Link
  Group = -> [LCS_Origin,Constraints,Variables,Configurations,Body]
  Origin = -> Origin
  Type = Assembly
---- part PlayStation5.FCStd = doc fcstd_5f6f5f70f897 ----
FCSTD DOCUMENT  (FreeCAD 0.20R29177 +426 (Git))
Label: PlayStation5
License: All rights reserved
LicenseURL: http://en.wikipedia.org/wiki/All_rights_reserved
objects: App::DocumentObjectGroup×3, PartDesign::CoordinateSystem×1, App::FeaturePython×1, Sketcher::SketchObject×1, PartDesign::Pad×1, PartDesign::Body×1, App::Part×1
note: 5 computed .brp shape members not serialized (recipe doc carries the construction recipe); baked Part::Feature solids carry a one-line shape summary decoded from their .brp

FEATURE [App::DocumentObjectGroup] Parts
FEATURE [PartDesign::CoordinateSystem] LCS_Origin
  AttacherType = Attacher::AttachEngine3D
  MapMode = 2
  Support = -> [X_Axis]
FEATURE [App::FeaturePython] Variables  # WARN: FeaturePython — macro-defined, semantics opaque (R4)
  Type = App::PropertyContainer
FEATURE [App::DocumentObjectGroup] Constraints
FEATURE [App::DocumentObjectGroup] Configurations
FEATURE [Sketcher::SketchObject] Sketch
  FullyConstrained = true
  MapMode = 5
  Support = -> [XY_Plane001]
  sketch-geometry (10):
    g0: ArcOfCircle CenterX=-119 CenterY=182.5 CenterZ=0 NormalX=0 NormalY=0 NormalZ=1 AngleXU=0 Radius=8 StartAngle=1.5708 EndAngle=3.14159
    g1: LineSegment StartX=-119 StartY=190.5 StartZ=0 EndX=119 EndY=190.5 EndZ=0
    g2: ArcOfCircle CenterX=119 CenterY=182.5 CenterZ=0 NormalX=0 NormalY=0 NormalZ=1 AngleXU=0 Radius=8 StartAngle=4.43e-14 EndAngle=1.5708
    g3: LineSegment StartX=127 StartY=182.5 StartZ=0 EndX=127 EndY=-182.5 EndZ=0
    g4: ArcOfCircle CenterX=119 CenterY=-182.5 CenterZ=0 NormalX=0 NormalY=0 NormalZ=1 AngleXU=0 Radius=8 StartAngle=4.71239 EndAngle=6.28319
    g5: LineSegment StartX=119 StartY=-190.5 StartZ=0 EndX=-119 EndY=-190.5 EndZ=0
    g6: ArcOfCircle CenterX=-119 CenterY=-182.5 CenterZ=0 NormalX=0 NormalY=0 NormalZ=1 AngleXU=0 Radius=8 StartAngle=3.14159 EndAngle=4.71239
    g7: LineSegment StartX=-127 StartY=-182.5 StartZ=0 EndX=-127 EndY=182.5 EndZ=0
    g8: GeomPoint X=-127 Y=190.5 Z=0
    g9: GeomPoint X=127 Y=-190.5 Z=0
  constraints (23):
    c: Tangent(g0,g1) = 1.5708
    c: Tangent(g1,g2) = 1.5708
    c: Tangent(g2,g3) = 1.5708
    c: Tangent(g3,g4) = 1.5708
    c: Tangent(g4,g5) = 1.5708
    c: Tangent(g5,g6) = 1.5708
    c: Tangent(g6,g7) = 1.5708
    c: Tangent(g7,g0) = 1.5708
    c: Horizontal(g1)
    c: Horizontal(g5)
    c: Vertical(g3)
    c: Vertical(g7)
    c: Equal(g0,g2)
    c: Equal(g2,g4)
    c: Equal(g4,g6)
    c: PointOnObject(g8,g1)
    c: PointOnObject(g8,g7)
    c: PointOnObject(g9,g3)
    c: PointOnObject(g9,g5)
    c: Symmetric(g4,g0,g-1)
    c: Radius(g2) = 8
    c: DistanceX(g6,g3) = 254
    c: DistanceY(g4,g1) = 381
FEATURE [PartDesign::Pad] Pad
  Direction = (0,0,1)
  Length = 82.55
  Length2 = 10
  Profile = -> Sketch
  ReferenceAxis = -> Sketch [N_Axis]
  Type = 0
FEATURE [PartDesign::Body] Body
  Group = -> [Sketch,Pad]
  Origin = -> Origin001
  Tip = -> Pad
FEATURE [App::Part] Assembly
  AssemblyType = Part::Link
  Group = -> [LCS_Origin,Variables,Constraints,Configurations,Body]
  Origin = -> Origin
  Type = Assembly
---- part SlipRing.FCStd = doc fcstd_f8d7c88fa0ad ----
FCSTD DOCUMENT  (FreeCAD 0.20R29177 +426 (Git))
Label: SlipRing
License: All rights reserved
LicenseURL: http://en.wikipedia.org/wiki/All_rights_reserved
objects: App::DocumentObjectGroup×3, PartDesign::CoordinateSystem×1, App::FeaturePython×1, Sketcher::SketchObject×1, PartDesign::Revolution×1, PartDesign::Body×1, App::Part×1
note: 5 computed .brp shape members not serialized (recipe doc carries the construction recipe); baked Part::Feature solids carry a one-line shape summary decoded from their .brp

FEATURE [App::DocumentObjectGroup] Parts
FEATURE [PartDesign::CoordinateSystem] LCS_Origin
  AttacherType = Attacher::AttachEngine3D
  MapMode = 2
  Support = -> [X_Axis]
FEATURE [App::FeaturePython] Variables  # WARN: FeaturePython — macro-defined, semantics opaque (R4)
  Type = App::PropertyContainer
FEATURE [App::DocumentObjectGroup] Constraints
FEATURE [App::DocumentObjectGroup] Configurations
FEATURE [Sketcher::SketchObject] Sketch
  FullyConstrained = true
  MapMode = 5
  Placement = pos=(0,0,0) rot=(1,0,0;1.5708rad)
  Support = -> [XZ_Plane001]
  sketch-geometry (14):
    g0: LineSegment StartX=0 StartY=38.6 StartZ=0 EndX=11 EndY=38.6 EndZ=0
    g1: LineSegment StartX=11 StartY=38.6 StartZ=0 EndX=11 EndY=0 EndZ=0
    g2: LineSegment StartX=11 StartY=0 StartZ=0 EndX=22.2 EndY=0 EndZ=0
    g3: LineSegment StartX=22.2 StartY=0 StartZ=0 EndX=22.2 EndY=-2.6 EndZ=0
    g4: LineSegment StartX=22.2 StartY=-2.6 StartZ=0 EndX=11 EndY=-2.6 EndZ=0
    g5: LineSegment StartX=11 StartY=-2.6 StartZ=0 EndX=11 EndY=-8.6 EndZ=0
    g6: LineSegment StartX=11 StartY=-8.6 StartZ=0 EndX=5 EndY=-8.6 EndZ=0
    g7: LineSegment StartX=5 StartY=-8.6 StartZ=0 EndX=5 EndY=-14.6 EndZ=0
    g8: LineSegment StartX=0 StartY=-14.6 StartZ=0 EndX=0 EndY=38.6 EndZ=0
    g9: LineSegment StartX=5 StartY=-14.6 StartZ=0 EndX=4 EndY=-14.6 EndZ=0
    g10: LineSegment StartX=4 StartY=-14.6 StartZ=0 EndX=0 EndY=-14.6 EndZ=0
    g11: LineSegment StartX=4 StartY=-14.6 StartZ=0 EndX=4 EndY=-30.6 EndZ=0
    g12: LineSegment StartX=4 StartY=-30.6 StartZ=0 EndX=0 EndY=-30.6 EndZ=0
    g13: LineSegment StartX=0 StartY=-30.6 StartZ=0 EndX=0 EndY=-14.6 EndZ=0
  constraints (41):
    c: PointOnObject(g0,g-2)
    c: Horizontal(g0)
    c: Coincident(g0,g1)
    c: Vertical(g1)
    c: Coincident(g1,g2)
    c: Horizontal(g2)
    c: Coincident(g2,g3)
    c: Vertical(g3)
    c: Coincident(g3,g4)
    c: Horizontal(g4)
    c: Coincident(g4,g5)
    c: Vertical(g5)
    c: Coincident(g5,g6)
    c: Coincident(g6,g7)
    c: Vertical(g7)
    c: Coincident(g7,g9)
    c: PointOnObject(g10,g-2)
    c: Coincident(g10,g8)
    c: Coincident(g8,g0)
    c: Horizontal(g6)
    c: DistanceX(g0,g0) = 11
    c: DistanceX(g-1,g3) = 22.2
    c: PointOnObject(g1,g5)
    c: DistanceX(g10,g9) = 5
    c: DistanceY(g7,g7) = 6
    c: DistanceY(g5,g5) = 6
    c: DistanceY(g3,g3) = 2.6
    c: DistanceY(g1,g1) = 38.6
    c: PointOnObject(g1,g-1)
    c: Coincident(g9,g10)
    c: Horizontal(g9)
    c: Horizontal(g10)
    c: Coincident(g11,g9)
    c: Vertical(g11)
    c: Coincident(g12,g11)
    c: PointOnObject(g12,g-2)
    c: Horizontal(g12)
    c: Coincident(g13,g12)
    c: Coincident(g13,g8)
    c: DistanceX(g12,g12) = 4
    c: DistanceY(g13,g13) = 16
FEATURE [PartDesign::Revolution] Revolution
  Angle = 360
  Axis = (0,-2e-16,1)
  Base = (0,0,0)
  Placement = pos=(0,0,0) rot=(1,0,0;1.5708rad)
  Profile = -> Sketch
  ReferenceAxis = -> Sketch [V_Axis]
  Reversed = true
FEATURE [PartDesign::Body] Body
  Group = -> [Sketch,Revolution]
  Origin = -> Origin001
  Tip = -> Revolution
FEATURE [App::Part] Assembly
  AssemblyType = Part::Link
  Group = -> [LCS_Origin,Variables,Constraints,Configurations,Body]
  Origin = -> Origin
  Type = Assembly
---- part StrutChannelHalf.FCStd = doc fcstd_8fc0440cb6dc ----
FCSTD DOCUMENT  (FreeCAD 0.20R29177 +426 (Git))
Label: StrutChannelHalf
License: All rights reserved
LicenseURL: http://en.wikipedia.org/wiki/All_rights_reserved
objects: App::DocumentObjectGroup×3, PartDesign::CoordinateSystem×2, Sketcher::SketchObject×2, App::FeaturePython×1, PartDesign::Pad×1, PartDesign::Pocket×1, PartDesign::LinearPattern×1, PartDesign::Mirrored×1, PartDesign::MultiTransform×1, PartDesign::Body×1, App::Part×1
note: 12 computed .brp shape members not serialized (recipe doc carries the construction recipe); baked Part::Feature solids carry a one-line shape summary decoded from their .brp

FEATURE [App::DocumentObjectGroup] Parts
FEATURE [PartDesign::CoordinateSystem] LCS_Origin
  AttacherType = Attacher::AttachEngine3D
  MapMode = 2
  Support = -> [X_Axis]
FEATURE [App::FeaturePython] Variables  # WARN: FeaturePython — macro-defined, semantics opaque (R4)
  Length = 600
  Type = App::PropertyContainer
FEATURE [App::DocumentObjectGroup] Constraints
FEATURE [App::DocumentObjectGroup] Configurations
FEATURE [Sketcher::SketchObject] Sketch
  FullyConstrained = true
  MapMode = 5
  Support = -> [XY_Plane001]
  sketch-geometry (22):
    g0: ArcOfCircle CenterX=-15.875 CenterY=15.8775 CenterZ=0 NormalX=0 NormalY=0 NormalZ=1 AngleXU=0 Radius=4.7625 StartAngle=-5.3e-15 EndAngle=3.14159
    g1: ArcOfCircle CenterX=15.875 CenterY=15.8775 CenterZ=0 NormalX=0 NormalY=0 NormalZ=1 AngleXU=0 Radius=4.7625 StartAngle=1e-16 EndAngle=3.14159
    g2: LineSegment StartX=20.6375 StartY=15.8775 StartZ=0 EndX=20.6375 EndY=1.5 EndZ=0
    g3: ArcOfCircle CenterX=19.1375 CenterY=1.5 CenterZ=0 NormalX=0 NormalY=0 NormalZ=1 AngleXU=0 Radius=1.5 StartAngle=4.71239 EndAngle=6.28319
    g4: LineSegment StartX=19.1375 StartY=0 StartZ=0 EndX=-19.1375 EndY=0 EndZ=0
    g5: ArcOfCircle CenterX=-19.1375 CenterY=1.5 CenterZ=0 NormalX=0 NormalY=0 NormalZ=1 AngleXU=0 Radius=1.5 StartAngle=3.14159 EndAngle=4.71239
    g6: LineSegment StartX=-20.6375 StartY=1.5 StartZ=0 EndX=-20.6375 EndY=15.8775 EndZ=0
    g7: GeomPoint X=20.6375 Y=0 Z=0
    g8: ArcOfCircle CenterX=-15.875 CenterY=15.8775 CenterZ=0 NormalX=0 NormalY=0 NormalZ=1 AngleXU=0 Radius=2.86512 StartAngle=-8e-15 EndAngle=3.14159
    g9: ArcOfCircle CenterX=15.875 CenterY=15.8775 CenterZ=0 NormalX=0 NormalY=0 NormalZ=1 AngleXU=0 Radius=2.86512 StartAngle=1e-16 EndAngle=3.14159
    g10: LineSegment StartX=18.7401 StartY=15.8775 StartZ=0 EndX=18.7401 EndY=2.89738 EndZ=0
    g11: ArcOfCircle CenterX=17.7401 CenterY=2.89738 CenterZ=0 NormalX=0 NormalY=0 NormalZ=1 AngleXU=0 Radius=1 StartAngle=4.71239 EndAngle=6.28319
    g12: LineSegment StartX=17.7401 StartY=1.89738 StartZ=0 EndX=-17.7401 EndY=1.89738 EndZ=0
    g13: ArcOfCircle CenterX=-17.7401 CenterY=2.89738 CenterZ=0 NormalX=0 NormalY=0 NormalZ=1 AngleXU=0 Radius=1 StartAngle=3.14159 EndAngle=4.71239
    g14: LineSegment StartX=-18.7401 StartY=2.89738 StartZ=0 EndX=-18.7401 EndY=15.8775 EndZ=0
    g15: GeomPoint X=18.7401 Y=1.89738 Z=0
    g16: GeomPoint X=1.3e-15 Y=1.89738 Z=0
    g17: LineSegment StartX=1.3e-15 StartY=1.89738 StartZ=0 EndX=0 EndY=0 EndZ=0
    g18: LineSegment StartX=18.7401 StartY=15.8775 StartZ=0 EndX=20.6375 EndY=15.8775 EndZ=0
    g19: LineSegment StartX=-13.0099 StartY=15.8775 StartZ=0 EndX=-11.1125 EndY=15.8775 EndZ=0
    g20: LineSegment StartX=11.1125 StartY=15.8775 StartZ=0 EndX=13.0099 EndY=15.8775 EndZ=0
    g21: LineSegment StartX=-15.875 StartY=20.64 StartZ=0 EndX=15.875 EndY=20.64 EndZ=0
  constraints (54):
    c: Tangent(g1,g2) = 1.5708
    c: Tangent(g2,g3) = 1.5708
    c: Tangent(g3,g4) = 1.5708
    c: Tangent(g4,g5) = 1.5708
    c: Tangent(g5,g6) = 1.5708
    c: Tangent(g6,g0) = 1.5708
    c: Horizontal(g4)
    c: Vertical(g2)
    c: Vertical(g6)
    c: Equal(g0,g1)
    c: Equal(g3,g5)
    c: PointOnObject(g7,g2)
    c: PointOnObject(g7,g4)
    c: Symmetric(g4,g3,g-1)
    c: Radius(g3) = 1.5
    c: Radius(g1) = 4.7625
    c: Tangent(g9,g10) = 1.5708
    c: Tangent(g10,g11) = 1.5708
    c: Tangent(g11,g12) = 1.5708
    c: Tangent(g12,g13) = 1.5708
    c: Tangent(g13,g14) = 1.5708
    c: Tangent(g14,g8) = 1.5708
    c: Horizontal(g12)
    c: Vertical(g10)
    c: Vertical(g14)
    c: Equal(g8,g9)
    c: Equal(g11,g13)
    c: PointOnObject(g15,g10)
    c: PointOnObject(g15,g12)
    c: Symmetric(g12,g11,g16)
    c: Coincident(g17,g16)
    c: Coincident(g17,g-1)
    c: DistanceY(g17,g17) = 1.89738
    c: Coincident(g18,g9)
    c: PointOnObject(g18,g2)
    c: Horizontal(g18)
    c: Equal(g18,g17)
    c: Coincident(g9,g1)
    c: Coincident(g8,g0)
    c: PointOnObject(g9,g18)
    c: PointOnObject(g8,g18)
    c: PointOnObject(g1,g18)
    c: PointOnObject(g0,g18)
    c: Coincident(g19,g8)
    c: Coincident(g19,g0)
    c: Coincident(g20,g1)
    c: Coincident(g20,g9)
    c: PointOnObject(g8,g19)
    c: DistanceX(g5,g2) = 41.275
    c: PointOnObject(g21,g0)
    c: Horizontal(g21)
    c: Tangent(g21,g1) = 1.5708
    c: DistanceY(g17,g21) = 20.64  'Height'
    c: Radius(g11) = 1
FEATURE [PartDesign::Pad] Pad
  Direction = (0,0,1)
  Length = 600
  Length2 = 10
  Midplane = true
  Profile = -> Sketch
  ReferenceAxis = -> Sketch [N_Axis]
  Type = 0
  expr: Length = <<Variables>>.Length
FEATURE [Sketcher::SketchObject] Sketch001
  FullyConstrained = true
  MapMode = 5
  Placement = pos=(0,0,0) rot=(1,0,0;1.5708rad)
  Support = -> [XZ_Plane001]
  sketch-geometry (5):
    g0: ArcOfCircle CenterX=0 CenterY=7.14125 CenterZ=0 NormalX=0 NormalY=0 NormalZ=1 AngleXU=0 Radius=7.14375 StartAngle=2.416e-13 EndAngle=3.14159
    g1: ArcOfCircle CenterX=0 CenterY=-7.14125 CenterZ=0 NormalX=0 NormalY=0 NormalZ=1 AngleXU=0 Radius=7.14375 StartAngle=3.14159 EndAngle=6.28319
    g2: LineSegment StartX=-7.14375 StartY=7.14125 StartZ=0 EndX=-7.14375 EndY=-7.14125 EndZ=0
    g3: LineSegment StartX=7.14375 StartY=-7.14125 StartZ=0 EndX=7.14375 EndY=7.14125 EndZ=0
    g4: LineSegment StartX=0 StartY=14.285 StartZ=0 EndX=0 EndY=-14.285 EndZ=0
  constraints (13):
    c: Tangent(g0,g2) = -1.5708
    c: Tangent(g2,g1) = -1.5708
    c: Tangent(g1,g3) = -1.5708
    c: Tangent(g3,g0) = -1.5708
    c: Equal(g0,g1)
    c: PointOnObject(g0,g-2)
    c: Symmetric(g0,g1,g-1)
    c: Diameter(g0) = 14.2875
    c: PointOnObject(g4,g0)
    c: PointOnObject(g4,g1)
    c: PointOnObject(g4,g-2)
    c: PointOnObject(g4,g-2)
    c: DistanceY(g4,g4) = 28.57
FEATURE [PartDesign::Pocket] Pocket  label="MountSlot"
  BaseFeature = -> Pad
  Direction = (0,1,2e-16)
  Length = 3
  Length2 = 5
  Profile = -> Sketch001
  ReferenceAxis = -> Sketch001 [N_Axis]
  Type = 0
FEATURE [PartDesign::LinearPattern] LinearPattern
  Direction = -> Sketch001 [V_Axis]
  Length = 355.6
  Occurrences = 8
  expr: Length = (ceil(<<Variables>>.Length / 2 / 50.8) + 1) * 50.8
  expr: Occurrences = ceil(<<Variables>>.Length / 2 / 50.8) + 2
FEATURE [PartDesign::Mirrored] Mirrored
  MirrorPlane = -> Sketch001 [H_Axis]
FEATURE [PartDesign::MultiTransform] MultiTransform
  BaseFeature = -> Pocket
  Originals = -> [Pocket]
  Transformations = -> [LinearPattern,Mirrored]
FEATURE [PartDesign::Body] Body
  Group = -> [Sketch,Pad,Sketch001,Pocket,MultiTransform,LinearPattern,Mirrored]
  Origin = -> Origin001
  Tip = -> MultiTransform
FEATURE [PartDesign::CoordinateSystem] LCS_Face
  AttacherType = Attacher::AttachEngine3D
  AttachmentOffset = pos=(0,20.64,0) rot=(0,0,1;0rad)
  MapMode = 2
  Placement = pos=(0,20.64,0) rot=(0,0,1;0rad)
  Support = -> [LCS_Origin]
  expr: .AttachmentOffset.Base.y = <<Sketch>>.Constraints.Height
FEATURE [App::Part] Assembly
  AssemblyType = Part::Link
  Group = -> [LCS_Origin,Variables,Constraints,Configurations,Body,LCS_Face]
  Origin = -> Origin
  Type = Assembly
